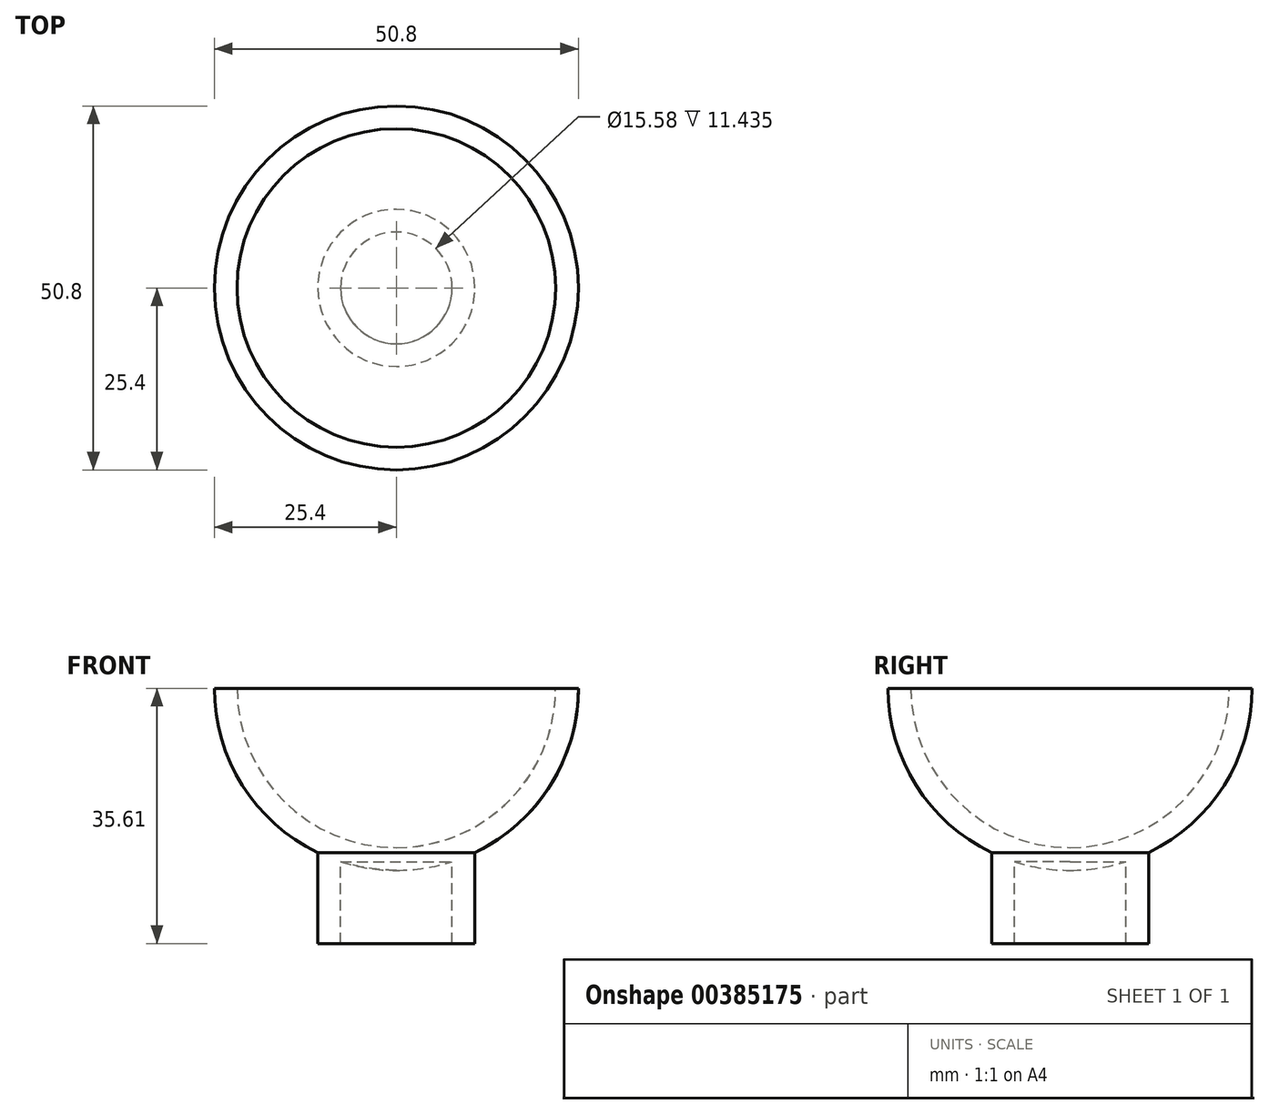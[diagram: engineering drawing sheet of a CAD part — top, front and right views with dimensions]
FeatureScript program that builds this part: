
annotation { "Feature Type Name" : "Feature", "Feature Type Description" : "" }
export const myFeature = defineFeature(function(context is Context, id is Id, definition is map)
    precondition{}
    {
        {
            var Q0;
            Q0=qCreatedBy(makeId("Front.planeOp"),FACE);
            var sketch = newSketch(context, id + "F0", { "sketchPlane" : qUnion([Q0])});
            skArc(sketch, "E0", {"start": v(0, -25.4) * mm, "mid": v(17.96, -17.96) * mm, "end": v(25.4, 0) * mm});
            skArc(sketch, "E1", {"start": v(0, -22.23) * mm, "mid": v(15.72, -15.72) * mm, "end": v(22.23, 0) * mm});
            skLineSegment(sketch, "E2", {"start": v(0, -22.23) * mm, "end": v(0, -25.4) * mm});
            skLineSegment(sketch, "E3", {"start": v(25.4, 0) * mm, "end": v(22.23, 0) * mm});
            skLineSegment(sketch, "E4", {"start": v(10.97, -22.91) * mm, "end": v(10.97, -35.61) * mm});
            skLineSegment(sketch, "E5", {"start": v(10.97, -35.61) * mm, "end": v(7.8, -35.61) * mm});
            skLineSegment(sketch, "E6", {"start": v(7.8, -35.61) * mm, "end": v(7.8, -24.18) * mm});
            skSolve(sketch);
        }
        {
            var Q0;
            Q0=makeQuery(id+"F0.imprint","IMPRINT",FACE,{"disambiguationData":[TD([[makeQuery(id+"F0.imprint","IMPRINT",EDGE,{"derivedFrom":sQuery(id+"F0.wireOp",EDGE,"E1")}),-1.0]])]});
            var Q1;
            {var subQ0=sQuery(id+"F0.wireOp",EDGE,"E4");Q1=makeQuery(id+"F0.imprint","IMPRINT",FACE,{"disambiguationData":[TD([[makeQuery(id+"F0.imprint","IMPRINT",EDGE,{"derivedFrom":subQ0}),-1.0]])]});}
            var Q2;
            Q2=sQuery(id+"F0.wireOp",EDGE,"E2");
            revolve(context, id + "F1", {"entities" : qUnion([Q0, Q1]), "axis" : qUnion([Q2]), "revolveType" : RevolveType.FULL});
        }
    });
